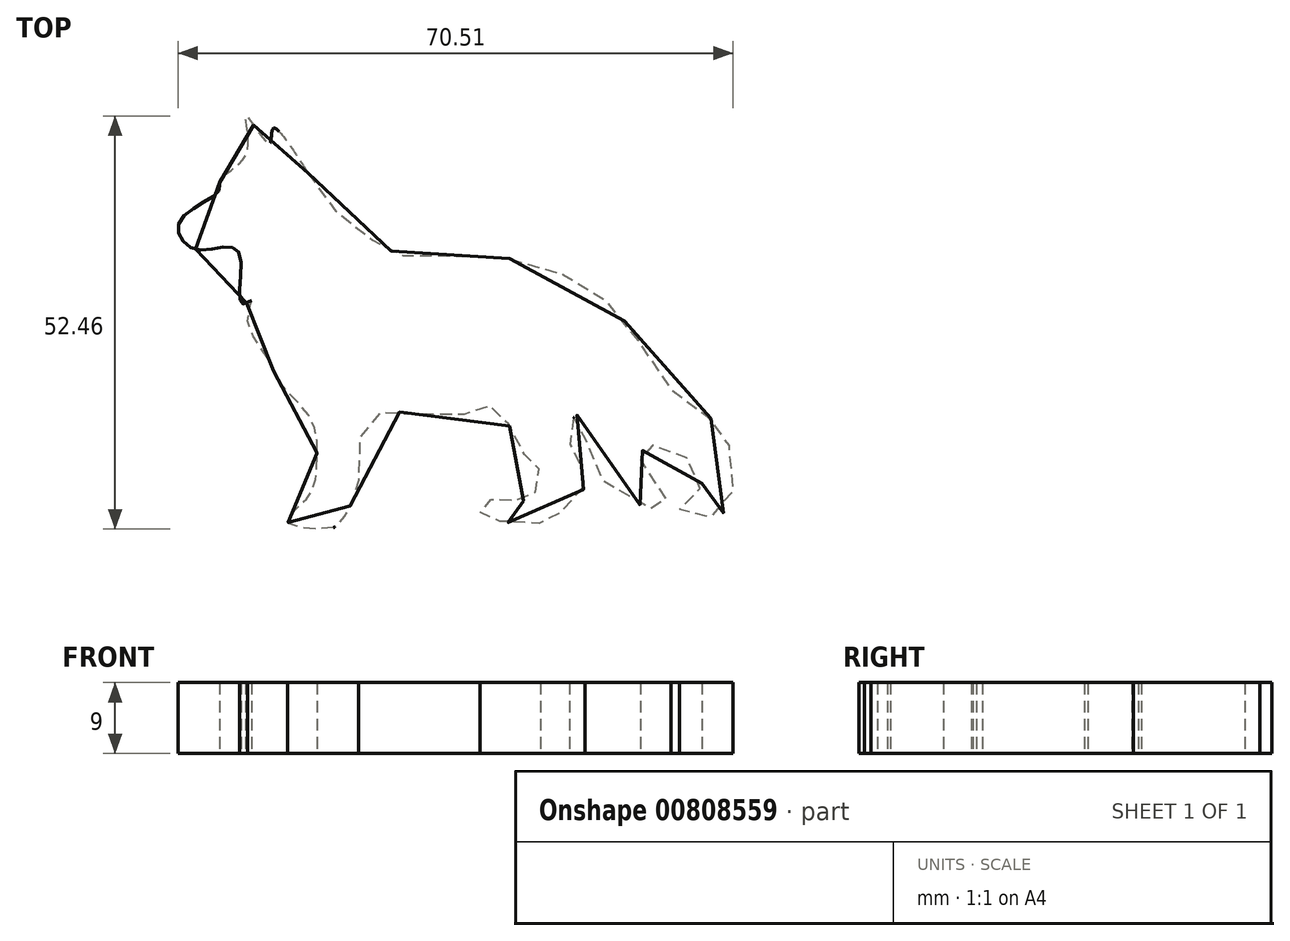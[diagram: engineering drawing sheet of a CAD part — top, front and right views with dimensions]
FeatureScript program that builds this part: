
annotation { "Feature Type Name" : "Feature", "Feature Type Description" : "" }
export const myFeature = defineFeature(function(context is Context, id is Id, definition is map)
    precondition{}
    {
        {
            var Q0;
            Q0=qCreatedBy(makeId("Top.planeOp"),FACE);
            var sketch = newSketch(context, id + "F0", { "sketchPlane" : qUnion([Q0])});
            skFitSpline(sketch, "E0", {"points": [v(-55.53, 47.71) * mm, v(-50.96, 41.92) * mm, v(-45, 37.84) * mm, v(-42.4, 37.16) * mm, v(-32.04, 37.18) * mm, v(-20.91, 33.78) * mm, v(-14.84, 28.26) * mm, v(-7.96, 18.75) * mm, v(-3.37, 15.78) * mm, v(-1.62, 10.2) * mm, v(-2.77, 4.57) * mm, v(-7.58, 4.48) * mm, v(-8.3, 5.28) * mm, v(-5.65, 7.81) * mm, v(-7.17, 11.41) * mm, v(-11.66, 13.14) * mm, v(-12.65, 13.06) * mm, v(-13.09, 10.24) * mm, v(-9.42, 5.11) * mm, v(-16.15, 6.94) * mm, v(-20.12, 13.36) * mm, v(-21.5, 17) * mm, v(-22.22, 13.1) * mm, v(-20.68, 10.25) * mm, v(-20.83, 7.01) * mm, v(-22.8, 5.73) * mm, v(-24.22, 3.76) * mm, v(-32.56, 3.86) * mm, v(-33.64, 4.92) * mm, v(-31.57, 6.48) * mm, v(-27.59, 6.27) * mm, v(-26.05, 9.84) * mm, v(-27.93, 11.88) * mm, v(-31.7, 17.98) * mm, v(-36.85, 16.87) * mm, v(-47.98, 16.46) * mm, v(-49.36, 6.48) * mm, v(-50.7, 5.01) * mm, v(-51.03, 3.74) * mm, v(-52.35, 2.7) * mm, v(-58.02, 3.33) * mm, v(-56.6, 5.48) * mm, v(-54.8, 7.88) * mm, v(-54.38, 12.1) * mm, v(-55.15, 16.46) * mm, v(-59.4, 21.52) * mm, v(-60.3, 23.7) * mm, v(-63.2, 29.16) * mm, v(-62.73, 31.56) * mm, v(-63.95, 31.17) * mm, v(-64.41, 37.83) * mm, v(-69.76, 38.06) * mm, v(-71.85, 41.52) * mm, v(-66.93, 45.4) * mm, v(-66.66, 46.93) * mm, v(-63.29, 50.46) * mm, v(-63.35, 54.96) * mm, v(-60.45, 51.51) * mm, v(-60, 53.38) * mm, v(-55.53, 47.71) * mm]});
            skSolve(sketch);
        }
        {
            var Q0;
            Q0=qSketchRegion(id+"F0",true);
            extrude(context, id + "F1", {"entities" : qUnion([Q0]), "depth" : 9 * mm, "offsetDistance" : 25.4 * mm});
        }
    });
